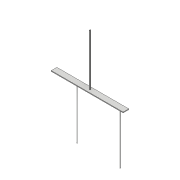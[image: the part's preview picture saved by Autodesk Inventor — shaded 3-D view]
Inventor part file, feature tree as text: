
AUTODESK INVENTOR PART (.ipt)
format: ipt  version: 2017 (Build 210142000, 142)  size: 115,200 bytes
history: native  units: mm
features: extrude x6, sketch x4, fillet x1, plane x1
ambient origin geometry x8: Origin, YZ Plane, XZ Plane, XY Plane, X Axis, Y Axis, Z Axis, Center Point
bodies: Solid1 (feature_tree)
feature tree (12):
  extrude  "Extrusion1"  Depth=3.25mm
  fillet  "Fillet2"  Radius=20.0mm
  plane  "Work Plane1"
  extrude  "Extrusion2"  Depth=8.25mm TaperAngle=0.0deg
  extrude  "Extrusion3"  Depth=70.0mm
  extrude  "Extrusion4"  Depth=10.0mm TaperAngle=0.0deg
  sketch  "Sketch5"  dims[d14=10.0mm d15=10.0mm d16=0.0mm d17=658.25mm d18=0.0mm]
  extrude  "Extrusion5"  Depth=658.25mm TaperAngle=0.0deg
  extrude  "Extrusion6"  [1 undecoded]
  sketch  "Sketch2"  dims[d0=650.0mm d1=0.0mm d4=3.25mm d5=20.0mm d6=0.0mm]
  sketch  "Sketch3"  dims[d7=25.5mm d8=0.0mm d9=8.25mm d10=0.0mm]
  sketch  "Sketch4"  dims[d11=900.0mm d12=70.0mm]
note: 1 required parameter value undecoded (feature->parameter linkage not recoverable at this tier; creation-order binding heuristic only, values carry confidence <= 0.55)
